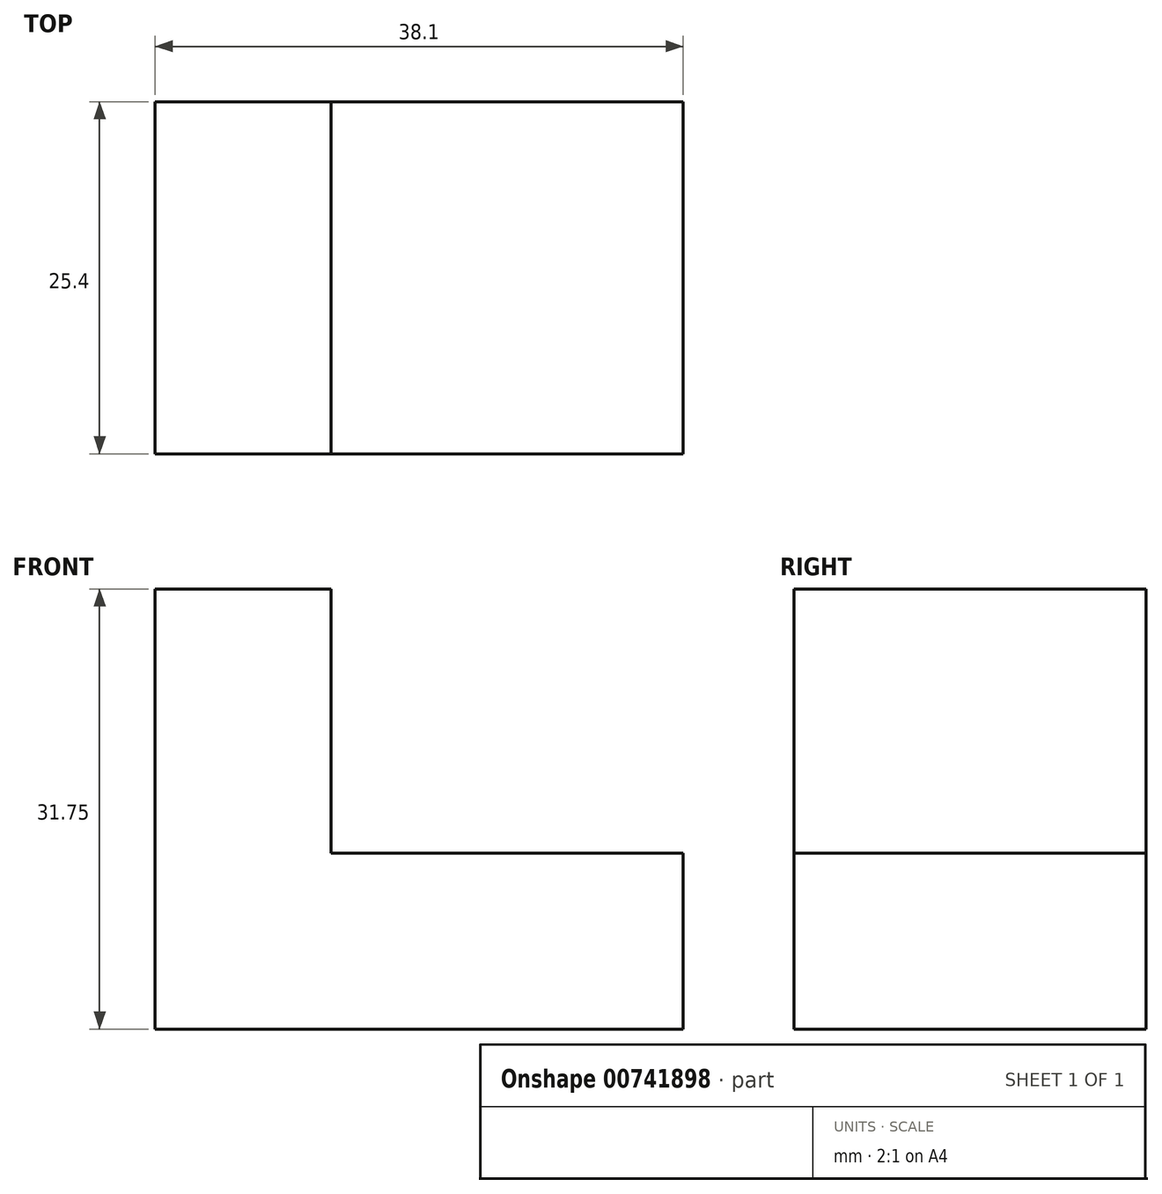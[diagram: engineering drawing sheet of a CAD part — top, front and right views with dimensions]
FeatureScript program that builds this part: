
annotation { "Feature Type Name" : "Feature", "Feature Type Description" : "" }
export const myFeature = defineFeature(function(context is Context, id is Id, definition is map)
    precondition{}
    {
        {
            var Q0;
            Q0=qCreatedBy(makeId("Front.planeOp"),FACE);
            var sketch = newSketch(context, id + "F0", { "sketchPlane" : qUnion([Q0])});
            skLineSegment(sketch, "E0", {"start": v(0, 31.75) * mm, "end": v(0, 0) * mm});
            skLineSegment(sketch, "E1", {"start": v(0, 0) * mm, "end": v(38.1, 0) * mm});
            skLineSegment(sketch, "E2", {"start": v(0, 31.75) * mm, "end": v(12.7, 31.75) * mm});
            skLineSegment(sketch, "E3", {"start": v(12.7, 31.75) * mm, "end": v(12.7, 12.7) * mm});
            skLineSegment(sketch, "E4", {"start": v(12.7, 12.7) * mm, "end": v(38.1, 12.7) * mm});
            skLineSegment(sketch, "E5", {"start": v(38.1, 12.7) * mm, "end": v(38.1, 0) * mm});
            skSolve(sketch);
        }
        {
            var Q0;
            Q0 = qSketchRegion(id + "F0", true);
            extrude(context, id + "F1", {"entities" : qUnion([Q0]), "depth" : 25.4 * mm, "offsetDistance" : 25.4 * mm});
        }
    });
